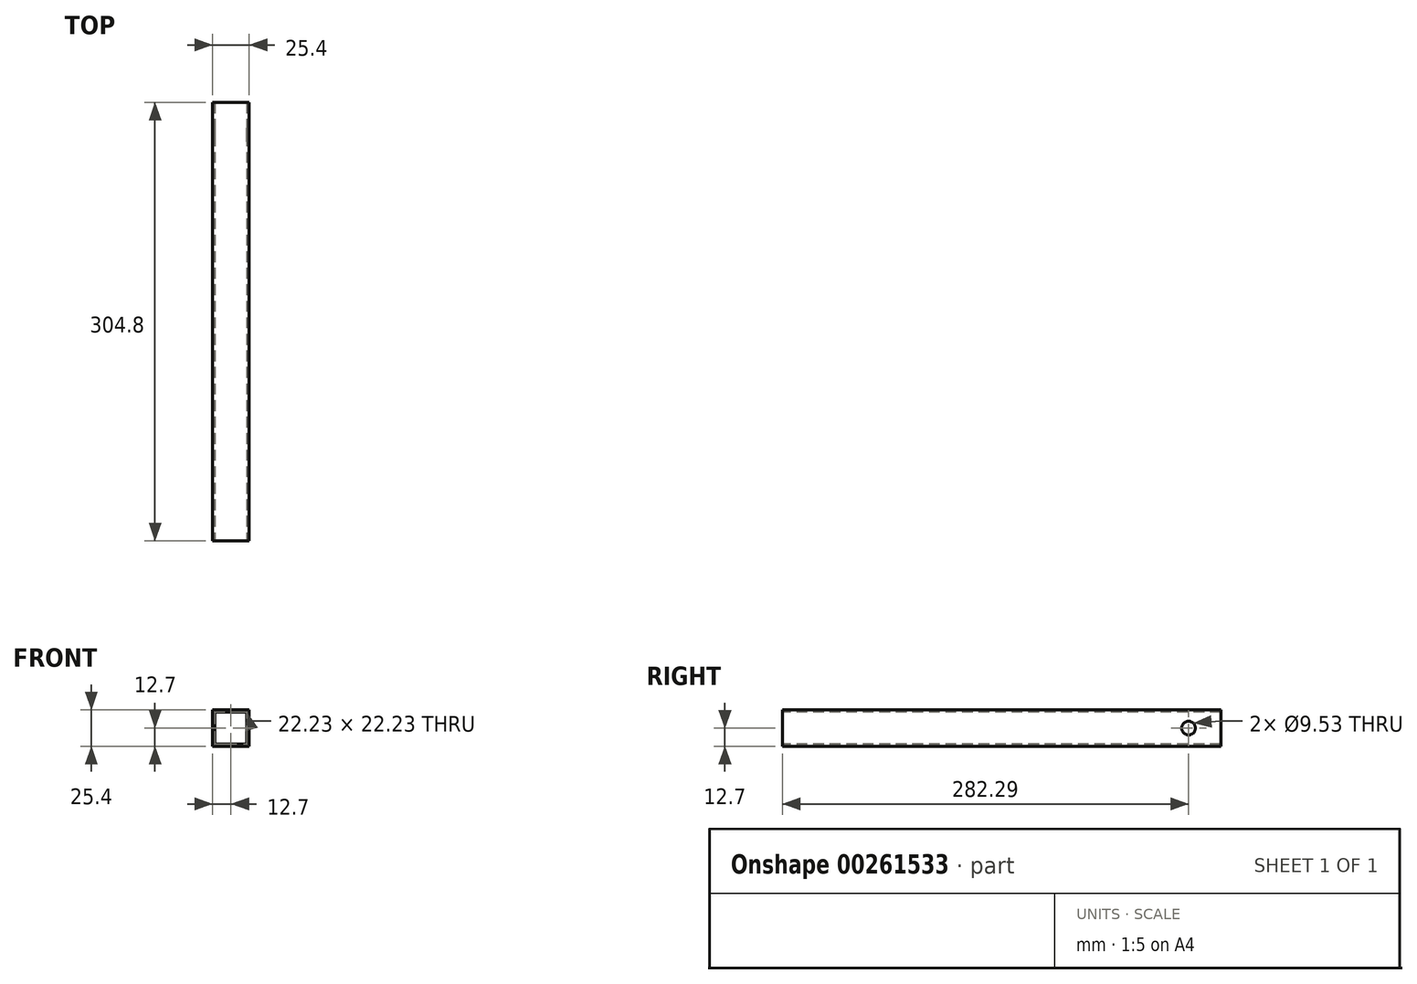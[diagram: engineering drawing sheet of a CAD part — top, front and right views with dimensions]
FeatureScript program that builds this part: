
annotation { "Feature Type Name" : "Feature", "Feature Type Description" : "" }
export const myFeature = defineFeature(function(context is Context, id is Id, definition is map)
    precondition{}
    {
        {
            var Q0;
            Q0=qCreatedBy(makeId("Top.planeOp"),FACE);
            var sketch = newSketch(context, id + "F0", { "sketchPlane" : qUnion([Q0])});
            skLineSegment(sketch, "E0.bottom", {"start": v(-12.7, 152.4) * mm, "end": v(12.7, 152.4) * mm});
            skLineSegment(sketch, "E0.top", {"start": v(-12.7, -152.4) * mm, "end": v(12.7, -152.4) * mm});
            skLineSegment(sketch, "E0.left", {"start": v(-12.7, 152.4) * mm, "end": v(-12.7, -152.4) * mm});
            skLineSegment(sketch, "E0.right", {"start": v(12.7, 152.4) * mm, "end": v(12.7, -152.4) * mm});
            skPoint(sketch, "E0.middle", {"position": v(0, 0) * mm});
            skSolve(sketch);
        }
        {
            var Q0;
            Q0=makeQuery(id+"F0.imprint","IMPRINT",FACE,{"disambiguationData":[TD([[makeQuery(id+"F0.imprint","IMPRINT",EDGE,{"derivedFrom":sQuery(id+"F0.wireOp",EDGE,"E0.bottom")}),-1.0]])]});
            extrude(context, id + "F1", {"entities" : qUnion([Q0]), "depth" : 25.4 * mm});
        }
        {
            var Q0;
            Q0=makeQuery(id+"F1.opExtrude","SWEPT_FACE",FACE,{"disambiguationData":[OSD([sQuery(id+"F0.wireOp",EDGE,"E0.top")])]});
            var Q1;
            Q1=makeQuery(id+"F1.opExtrude","SWEPT_FACE",FACE,{"disambiguationData":[OSD([sQuery(id+"F0.wireOp",EDGE,"E0.bottom")])]});
            shell(context, id + "F2", {"entities" : qUnion([Q0, Q1]), "thickness" : 1.59 * mm});
        }
        {
            var Q0;
            Q0=makeQuery(id+"F1.opExtrude","SWEPT_FACE",FACE,{"disambiguationData":[OSD([sQuery(id+"F0.wireOp",EDGE,"E0.right")])]});
            var sketch = newSketch(context, id + "F3", { "sketchPlane" : qUnion([Q0])});
            skCircle(sketch, "E1", {"center": v(129.9, 12.7) * mm, "radius": 5.33 * mm});
            skSolve(sketch);
        }
        {
            var Q0;
            Q0=sQuery(id+"F3.wireOp",VERTEX,"E1.center");
            var Q1;
            Q1=makeQuery(id+"F1.opExtrude","SWEPT_BODY",BODY,{"disambiguationData":[OSD([sQuery(id+"F0.wireOp",EDGE,"E0.bottom"),sQuery(id+"F0.wireOp",EDGE,"E0.top"),sQuery(id+"F0.wireOp",EDGE,"E0.left"),sQuery(id+"F0.wireOp",EDGE,"E0.right")])]});
            hole(context, id + "F4", {"style" : HoleStyle.SIMPLE, "endStyle" : HoleEndStyle.THROUGH, "holeDiameter" : 9.52 * mm, "tappedDepth" : 12.7 * mm, "tapClearance" : 3, "locations" : qUnion([Q0]), "scope" : qUnion([Q1])});
        }
    });
